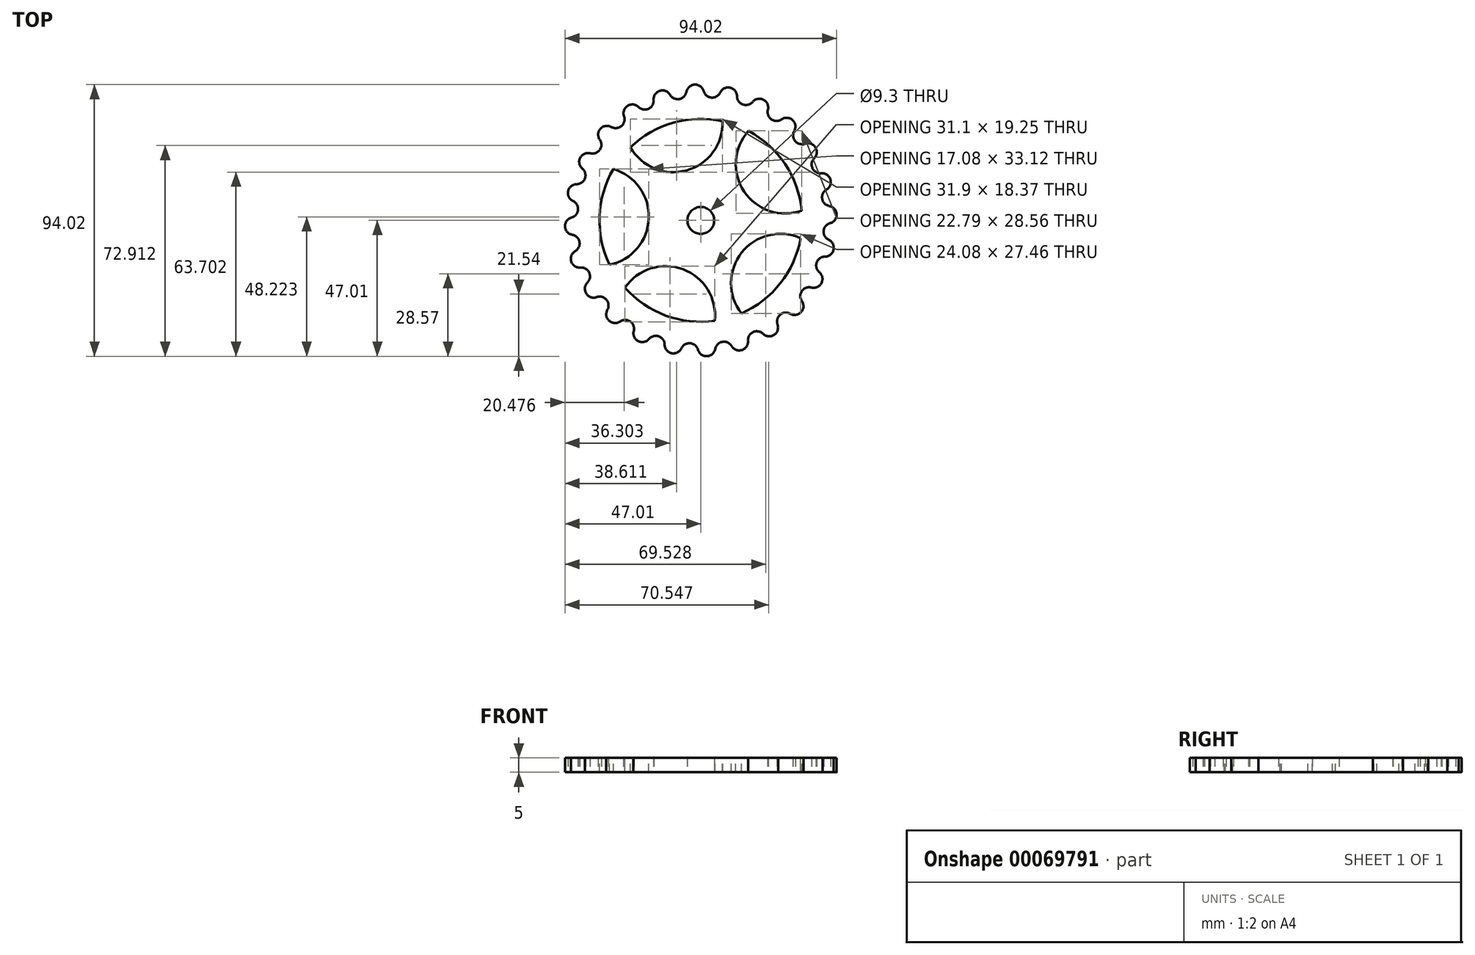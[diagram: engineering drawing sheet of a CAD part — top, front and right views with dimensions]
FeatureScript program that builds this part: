
annotation { "Feature Type Name" : "Feature", "Feature Type Description" : "" }
export const myFeature = defineFeature(function(context is Context, id is Id, definition is map)
    precondition{}
    {
        {
            var Q0;
            Q0=qCreatedBy(makeId("Top.planeOp"),FACE);
            var sketch = newSketch(context, id + "F0", { "sketchPlane" : qUnion([Q0])});
            skArc(sketch, "E0", {"start": v(0.98, 44.76) * mm, "mid": v(-0.17, 46.42) * mm, "end": v(-2.1, 47) * mm});
            skArc(sketch, "E1", {"start": v(0.98, 44.76) * mm, "mid": v(1.97, 43.21) * mm, "end": v(3.67, 42.51) * mm});
            skLineSegment(sketch, "E2", {"start": v(0, 0) * mm, "end": v(3.93, 45.56) * mm, "construction": true});
            skLineSegment(sketch, "E3", {"start": v(0, 0) * mm, "end": v(-1.97, 43.95) * mm, "construction": true});
            skLineSegment(sketch, "E4", {"start": v(-1.97, 43.95) * mm, "end": v(-2.18, 48.5) * mm, "construction": true});
            skArc(sketch, "E5.MirrorCS", {"start": v(6.7, 44.26) * mm, "mid": v(5.46, 42.91) * mm, "end": v(3.67, 42.51) * mm});
            skArc(sketch, "E6.MirrorCS", {"start": v(6.7, 44.26) * mm, "mid": v(8.12, 45.7) * mm, "end": v(10.13, 45.95) * mm});
            skArc(sketch, "E7.1.0", {"start": v(-10.64, 43.49) * mm, "mid": v(-12.18, 44.8) * mm, "end": v(-14.2, 44.86) * mm});
            skArc(sketch, "E7.1.1", {"start": v(-10.64, 43.49) * mm, "mid": v(-9.28, 42.25) * mm, "end": v(-7.46, 42.02) * mm});
            skArc(sketch, "E7.1.2", {"start": v(-4.98, 44.49) * mm, "mid": v(-5.83, 42.86) * mm, "end": v(-7.46, 42.02) * mm});
            skArc(sketch, "E7.1.3", {"start": v(-4.98, 44.49) * mm, "mid": v(-3.99, 46.25) * mm, "end": v(-2.1, 47) * mm});
            skArc(sketch, "E7.2.0", {"start": v(-21.53, 39.25) * mm, "mid": v(-23.36, 40.12) * mm, "end": v(-25.33, 39.66) * mm});
            skArc(sketch, "E7.2.1", {"start": v(-21.53, 39.25) * mm, "mid": v(-19.9, 38.4) * mm, "end": v(-18.08, 38.65) * mm});
            skArc(sketch, "E7.2.2", {"start": v(-16.33, 41.68) * mm, "mid": v(-16.73, 39.9) * mm, "end": v(-18.08, 38.65) * mm});
            skArc(sketch, "E7.2.3", {"start": v(-16.33, 41.68) * mm, "mid": v(-15.82, 43.65) * mm, "end": v(-14.2, 44.86) * mm});
            skArc(sketch, "E7.3.0", {"start": v(-30.96, 32.34) * mm, "mid": v(-32.95, 32.7) * mm, "end": v(-34.73, 31.75) * mm});
            skArc(sketch, "E7.3.1", {"start": v(-30.96, 32.34) * mm, "mid": v(-29.16, 31.95) * mm, "end": v(-27.47, 32.66) * mm});
            skArc(sketch, "E7.3.2", {"start": v(-26.56, 36.04) * mm, "mid": v(-26.48, 34.2) * mm, "end": v(-27.47, 32.66) * mm});
            skArc(sketch, "E7.3.3", {"start": v(-26.56, 36.04) * mm, "mid": v(-26.58, 38.06) * mm, "end": v(-25.33, 39.66) * mm});
            skArc(sketch, "E7.4.0", {"start": v(-38.27, 23.23) * mm, "mid": v(-40.29, 23.07) * mm, "end": v(-41.76, 21.68) * mm});
            skArc(sketch, "E7.4.1", {"start": v(-38.27, 23.23) * mm, "mid": v(-36.44, 23.31) * mm, "end": v(-34.98, 24.43) * mm});
            skArc(sketch, "E7.4.2", {"start": v(-34.98, 27.94) * mm, "mid": v(-34.43, 26.18) * mm, "end": v(-34.98, 24.43) * mm});
            skArc(sketch, "E7.4.3", {"start": v(-34.98, 27.94) * mm, "mid": v(-35.53, 29.89) * mm, "end": v(-34.73, 31.75) * mm});
            skArc(sketch, "E7.5.0", {"start": v(-42.98, 12.53) * mm, "mid": v(-44.89, 11.85) * mm, "end": v(-45.95, 10.13) * mm});
            skArc(sketch, "E7.5.1", {"start": v(-42.98, 12.53) * mm, "mid": v(-41.23, 13.09) * mm, "end": v(-40.12, 14.55) * mm});
            skArc(sketch, "E7.5.2", {"start": v(-41.02, 17.93) * mm, "mid": v(-40.04, 16.38) * mm, "end": v(-40.12, 14.55) * mm});
            skArc(sketch, "E7.5.3", {"start": v(-41.02, 17.93) * mm, "mid": v(-42.05, 19.67) * mm, "end": v(-41.76, 21.68) * mm});
            skArc(sketch, "E7.6.0", {"start": v(-44.76, 0.98) * mm, "mid": v(-46.42, -0.17) * mm, "end": v(-47, -2.1) * mm});
            skArc(sketch, "E7.6.1", {"start": v(-44.76, 0.98) * mm, "mid": v(-43.21, 1.97) * mm, "end": v(-42.51, 3.67) * mm});
            skArc(sketch, "E7.6.2", {"start": v(-44.26, 6.7) * mm, "mid": v(-42.91, 5.46) * mm, "end": v(-42.51, 3.67) * mm});
            skArc(sketch, "E7.6.3", {"start": v(-44.26, 6.7) * mm, "mid": v(-45.7, 8.12) * mm, "end": v(-45.95, 10.13) * mm});
            skArc(sketch, "E7.7.0", {"start": v(-43.49, -10.64) * mm, "mid": v(-44.8, -12.18) * mm, "end": v(-44.86, -14.2) * mm});
            skArc(sketch, "E7.7.1", {"start": v(-43.49, -10.64) * mm, "mid": v(-42.25, -9.28) * mm, "end": v(-42.02, -7.46) * mm});
            skArc(sketch, "E7.7.2", {"start": v(-44.49, -4.98) * mm, "mid": v(-42.86, -5.83) * mm, "end": v(-42.02, -7.46) * mm});
            skArc(sketch, "E7.7.3", {"start": v(-44.49, -4.98) * mm, "mid": v(-46.25, -3.99) * mm, "end": v(-47, -2.1) * mm});
            skArc(sketch, "E7.8.0", {"start": v(-39.25, -21.53) * mm, "mid": v(-40.12, -23.36) * mm, "end": v(-39.66, -25.33) * mm});
            skArc(sketch, "E7.8.1", {"start": v(-39.25, -21.53) * mm, "mid": v(-38.4, -19.9) * mm, "end": v(-38.65, -18.08) * mm});
            skArc(sketch, "E7.8.2", {"start": v(-41.68, -16.33) * mm, "mid": v(-39.9, -16.73) * mm, "end": v(-38.65, -18.08) * mm});
            skArc(sketch, "E7.8.3", {"start": v(-41.68, -16.33) * mm, "mid": v(-43.65, -15.82) * mm, "end": v(-44.86, -14.2) * mm});
            skArc(sketch, "E7.9.0", {"start": v(-32.34, -30.96) * mm, "mid": v(-32.7, -32.95) * mm, "end": v(-31.75, -34.73) * mm});
            skArc(sketch, "E7.9.1", {"start": v(-32.34, -30.96) * mm, "mid": v(-31.95, -29.16) * mm, "end": v(-32.66, -27.47) * mm});
            skArc(sketch, "E7.9.2", {"start": v(-36.04, -26.56) * mm, "mid": v(-34.2, -26.48) * mm, "end": v(-32.66, -27.47) * mm});
            skArc(sketch, "E7.9.3", {"start": v(-36.04, -26.56) * mm, "mid": v(-38.06, -26.58) * mm, "end": v(-39.66, -25.33) * mm});
            skArc(sketch, "E7.10.0", {"start": v(-23.23, -38.27) * mm, "mid": v(-23.07, -40.29) * mm, "end": v(-21.68, -41.76) * mm});
            skArc(sketch, "E7.10.1", {"start": v(-23.23, -38.27) * mm, "mid": v(-23.31, -36.44) * mm, "end": v(-24.43, -34.98) * mm});
            skArc(sketch, "E7.10.2", {"start": v(-27.94, -34.98) * mm, "mid": v(-26.18, -34.43) * mm, "end": v(-24.43, -34.98) * mm});
            skArc(sketch, "E7.10.3", {"start": v(-27.94, -34.98) * mm, "mid": v(-29.89, -35.53) * mm, "end": v(-31.75, -34.73) * mm});
            skArc(sketch, "E7.11.0", {"start": v(-12.53, -42.98) * mm, "mid": v(-11.85, -44.89) * mm, "end": v(-10.13, -45.95) * mm});
            skArc(sketch, "E7.11.1", {"start": v(-12.53, -42.98) * mm, "mid": v(-13.09, -41.23) * mm, "end": v(-14.55, -40.12) * mm});
            skArc(sketch, "E7.11.2", {"start": v(-17.93, -41.02) * mm, "mid": v(-16.38, -40.04) * mm, "end": v(-14.55, -40.12) * mm});
            skArc(sketch, "E7.11.3", {"start": v(-17.93, -41.02) * mm, "mid": v(-19.67, -42.05) * mm, "end": v(-21.68, -41.76) * mm});
            skArc(sketch, "E7.12.0", {"start": v(-0.98, -44.76) * mm, "mid": v(0.17, -46.42) * mm, "end": v(2.1, -47) * mm});
            skArc(sketch, "E7.12.1", {"start": v(-0.98, -44.76) * mm, "mid": v(-1.97, -43.21) * mm, "end": v(-3.67, -42.51) * mm});
            skArc(sketch, "E7.12.2", {"start": v(-6.7, -44.26) * mm, "mid": v(-5.46, -42.91) * mm, "end": v(-3.67, -42.51) * mm});
            skArc(sketch, "E7.12.3", {"start": v(-6.7, -44.26) * mm, "mid": v(-8.12, -45.7) * mm, "end": v(-10.13, -45.95) * mm});
            skArc(sketch, "E7.13.0", {"start": v(10.64, -43.49) * mm, "mid": v(12.18, -44.8) * mm, "end": v(14.2, -44.86) * mm});
            skArc(sketch, "E7.13.1", {"start": v(10.64, -43.49) * mm, "mid": v(9.28, -42.25) * mm, "end": v(7.46, -42.02) * mm});
            skArc(sketch, "E7.13.2", {"start": v(4.98, -44.49) * mm, "mid": v(5.83, -42.86) * mm, "end": v(7.46, -42.02) * mm});
            skArc(sketch, "E7.13.3", {"start": v(4.98, -44.49) * mm, "mid": v(3.99, -46.25) * mm, "end": v(2.1, -47) * mm});
            skArc(sketch, "E7.14.0", {"start": v(21.53, -39.25) * mm, "mid": v(23.36, -40.12) * mm, "end": v(25.33, -39.66) * mm});
            skArc(sketch, "E7.14.1", {"start": v(21.53, -39.25) * mm, "mid": v(19.9, -38.4) * mm, "end": v(18.08, -38.65) * mm});
            skArc(sketch, "E7.14.2", {"start": v(16.33, -41.68) * mm, "mid": v(16.73, -39.9) * mm, "end": v(18.08, -38.65) * mm});
            skArc(sketch, "E7.14.3", {"start": v(16.33, -41.68) * mm, "mid": v(15.82, -43.65) * mm, "end": v(14.2, -44.86) * mm});
            skArc(sketch, "E7.15.0", {"start": v(30.96, -32.34) * mm, "mid": v(32.95, -32.7) * mm, "end": v(34.73, -31.75) * mm});
            skArc(sketch, "E7.15.1", {"start": v(30.96, -32.34) * mm, "mid": v(29.16, -31.95) * mm, "end": v(27.47, -32.66) * mm});
            skArc(sketch, "E7.15.2", {"start": v(26.56, -36.04) * mm, "mid": v(26.48, -34.2) * mm, "end": v(27.47, -32.66) * mm});
            skArc(sketch, "E7.15.3", {"start": v(26.56, -36.04) * mm, "mid": v(26.58, -38.06) * mm, "end": v(25.33, -39.66) * mm});
            skArc(sketch, "E7.16.0", {"start": v(38.27, -23.23) * mm, "mid": v(40.29, -23.07) * mm, "end": v(41.76, -21.68) * mm});
            skArc(sketch, "E7.16.1", {"start": v(38.27, -23.23) * mm, "mid": v(36.44, -23.31) * mm, "end": v(34.98, -24.43) * mm});
            skArc(sketch, "E7.16.2", {"start": v(34.98, -27.94) * mm, "mid": v(34.43, -26.18) * mm, "end": v(34.98, -24.43) * mm});
            skArc(sketch, "E7.16.3", {"start": v(34.98, -27.94) * mm, "mid": v(35.53, -29.89) * mm, "end": v(34.73, -31.75) * mm});
            skArc(sketch, "E7.17.0", {"start": v(42.98, -12.53) * mm, "mid": v(44.89, -11.85) * mm, "end": v(45.95, -10.13) * mm});
            skArc(sketch, "E7.17.1", {"start": v(42.98, -12.53) * mm, "mid": v(41.23, -13.09) * mm, "end": v(40.12, -14.55) * mm});
            skArc(sketch, "E7.17.2", {"start": v(41.02, -17.93) * mm, "mid": v(40.04, -16.38) * mm, "end": v(40.12, -14.55) * mm});
            skArc(sketch, "E7.17.3", {"start": v(41.02, -17.93) * mm, "mid": v(42.05, -19.67) * mm, "end": v(41.76, -21.68) * mm});
            skArc(sketch, "E7.18.0", {"start": v(44.76, -0.98) * mm, "mid": v(46.42, 0.17) * mm, "end": v(47, 2.1) * mm});
            skArc(sketch, "E7.18.1", {"start": v(44.76, -0.98) * mm, "mid": v(43.21, -1.97) * mm, "end": v(42.51, -3.67) * mm});
            skArc(sketch, "E7.18.2", {"start": v(44.26, -6.7) * mm, "mid": v(42.91, -5.46) * mm, "end": v(42.51, -3.67) * mm});
            skArc(sketch, "E7.18.3", {"start": v(44.26, -6.7) * mm, "mid": v(45.7, -8.12) * mm, "end": v(45.95, -10.13) * mm});
            skArc(sketch, "E7.19.0", {"start": v(43.49, 10.64) * mm, "mid": v(44.8, 12.18) * mm, "end": v(44.86, 14.2) * mm});
            skArc(sketch, "E7.19.1", {"start": v(43.49, 10.64) * mm, "mid": v(42.25, 9.28) * mm, "end": v(42.02, 7.46) * mm});
            skArc(sketch, "E7.19.2", {"start": v(44.49, 4.98) * mm, "mid": v(42.86, 5.83) * mm, "end": v(42.02, 7.46) * mm});
            skArc(sketch, "E7.19.3", {"start": v(44.49, 4.98) * mm, "mid": v(46.25, 3.99) * mm, "end": v(47, 2.1) * mm});
            skArc(sketch, "E7.20.0", {"start": v(39.25, 21.53) * mm, "mid": v(40.12, 23.36) * mm, "end": v(39.66, 25.33) * mm});
            skArc(sketch, "E7.20.1", {"start": v(39.25, 21.53) * mm, "mid": v(38.4, 19.9) * mm, "end": v(38.65, 18.08) * mm});
            skArc(sketch, "E7.20.2", {"start": v(41.68, 16.33) * mm, "mid": v(39.9, 16.73) * mm, "end": v(38.65, 18.08) * mm});
            skArc(sketch, "E7.20.3", {"start": v(41.68, 16.33) * mm, "mid": v(43.65, 15.82) * mm, "end": v(44.86, 14.2) * mm});
            skArc(sketch, "E7.21.0", {"start": v(32.34, 30.96) * mm, "mid": v(32.7, 32.95) * mm, "end": v(31.75, 34.73) * mm});
            skArc(sketch, "E7.21.1", {"start": v(32.34, 30.96) * mm, "mid": v(31.95, 29.16) * mm, "end": v(32.66, 27.47) * mm});
            skArc(sketch, "E7.21.2", {"start": v(36.04, 26.56) * mm, "mid": v(34.2, 26.48) * mm, "end": v(32.66, 27.47) * mm});
            skArc(sketch, "E7.21.3", {"start": v(36.04, 26.56) * mm, "mid": v(38.06, 26.58) * mm, "end": v(39.66, 25.33) * mm});
            skArc(sketch, "E7.22.0", {"start": v(23.23, 38.27) * mm, "mid": v(23.07, 40.29) * mm, "end": v(21.68, 41.76) * mm});
            skArc(sketch, "E7.22.1", {"start": v(23.23, 38.27) * mm, "mid": v(23.31, 36.44) * mm, "end": v(24.43, 34.98) * mm});
            skArc(sketch, "E7.22.2", {"start": v(27.94, 34.98) * mm, "mid": v(26.18, 34.43) * mm, "end": v(24.43, 34.98) * mm});
            skArc(sketch, "E7.22.3", {"start": v(27.94, 34.98) * mm, "mid": v(29.89, 35.53) * mm, "end": v(31.75, 34.73) * mm});
            skArc(sketch, "E7.23.0", {"start": v(12.53, 42.98) * mm, "mid": v(11.85, 44.89) * mm, "end": v(10.13, 45.95) * mm});
            skArc(sketch, "E7.23.1", {"start": v(12.53, 42.98) * mm, "mid": v(13.09, 41.23) * mm, "end": v(14.55, 40.12) * mm});
            skArc(sketch, "E7.23.2", {"start": v(17.93, 41.02) * mm, "mid": v(16.38, 40.04) * mm, "end": v(14.55, 40.12) * mm});
            skArc(sketch, "E7.23.3", {"start": v(17.93, 41.02) * mm, "mid": v(19.67, 42.05) * mm, "end": v(21.68, 41.76) * mm});
            skPoint(sketch, "E7.center", {"position": v(0, 0) * mm});
            skSolve(sketch);
        }
        {
            var Q0;
            Q0=makeQuery(id+"F0.imprint","IMPRINT",FACE,{"disambiguationData":[TD([[makeQuery(id+"F0.imprint","IMPRINT",EDGE,{"derivedFrom":sQuery(id+"F0.wireOp",EDGE,"E0")}),1.0]])]});
            extrude(context, id + "F1", {"entities" : qUnion([Q0]), "depth" : 5 * mm});
        }
        {
            var Q0;
            Q0=qCreatedBy(makeId("Top.planeOp"),FACE);
            var sketch = newSketch(context, id + "F2", { "sketchPlane" : qUnion([Q0])});
            skCircle(sketch, "E8", {"center": v(0, 0) * mm, "radius": 4.65 * mm});
            skSolve(sketch);
        }
        {
            var Q0;
            Q0 = qSketchRegion(id + "F2", true);
            extrude(context, id + "F3", {"entities" : qUnion([Q0]), "operationType" : NewBodyOperationType.REMOVE, "depth" : 25 * mm});
        }
        {
            var Q0;
            Q0=makeQuery(id+"F1.opExtrude","CAP_FACE",FACE,{"disambiguationData":[OSD([sQuery(id+"F0.wireOp",EDGE,"E0"),sQuery(id+"F0.wireOp",EDGE,"E1"),sQuery(id+"F0.wireOp",EDGE,"E5.MirrorCS"),sQuery(id+"F0.wireOp",EDGE,"E6.MirrorCS"),sQuery(id+"F0.wireOp",EDGE,"E7.1.0"),sQuery(id+"F0.wireOp",EDGE,"E7.1.1"),sQuery(id+"F0.wireOp",EDGE,"E7.1.2"),sQuery(id+"F0.wireOp",EDGE,"E7.1.3"),sQuery(id+"F0.wireOp",EDGE,"E7.2.0"),sQuery(id+"F0.wireOp",EDGE,"E7.2.1"),sQuery(id+"F0.wireOp",EDGE,"E7.2.2"),sQuery(id+"F0.wireOp",EDGE,"E7.2.3"),sQuery(id+"F0.wireOp",EDGE,"E7.3.0"),sQuery(id+"F0.wireOp",EDGE,"E7.3.1"),sQuery(id+"F0.wireOp",EDGE,"E7.3.2"),sQuery(id+"F0.wireOp",EDGE,"E7.3.3"),sQuery(id+"F0.wireOp",EDGE,"E7.4.0"),sQuery(id+"F0.wireOp",EDGE,"E7.4.1"),sQuery(id+"F0.wireOp",EDGE,"E7.4.2"),sQuery(id+"F0.wireOp",EDGE,"E7.4.3"),sQuery(id+"F0.wireOp",EDGE,"E7.5.0"),sQuery(id+"F0.wireOp",EDGE,"E7.5.1"),sQuery(id+"F0.wireOp",EDGE,"E7.5.2"),sQuery(id+"F0.wireOp",EDGE,"E7.5.3"),sQuery(id+"F0.wireOp",EDGE,"E7.6.0"),sQuery(id+"F0.wireOp",EDGE,"E7.6.1"),sQuery(id+"F0.wireOp",EDGE,"E7.6.2"),sQuery(id+"F0.wireOp",EDGE,"E7.6.3"),sQuery(id+"F0.wireOp",EDGE,"E7.7.0"),sQuery(id+"F0.wireOp",EDGE,"E7.7.1"),sQuery(id+"F0.wireOp",EDGE,"E7.7.2"),sQuery(id+"F0.wireOp",EDGE,"E7.7.3"),sQuery(id+"F0.wireOp",EDGE,"E7.8.0"),sQuery(id+"F0.wireOp",EDGE,"E7.8.1"),sQuery(id+"F0.wireOp",EDGE,"E7.8.2"),sQuery(id+"F0.wireOp",EDGE,"E7.8.3"),sQuery(id+"F0.wireOp",EDGE,"E7.9.0"),sQuery(id+"F0.wireOp",EDGE,"E7.9.1"),sQuery(id+"F0.wireOp",EDGE,"E7.9.2"),sQuery(id+"F0.wireOp",EDGE,"E7.9.3"),sQuery(id+"F0.wireOp",EDGE,"E7.10.0"),sQuery(id+"F0.wireOp",EDGE,"E7.10.1"),sQuery(id+"F0.wireOp",EDGE,"E7.10.2"),sQuery(id+"F0.wireOp",EDGE,"E7.10.3"),sQuery(id+"F0.wireOp",EDGE,"E7.11.0"),sQuery(id+"F0.wireOp",EDGE,"E7.11.1"),sQuery(id+"F0.wireOp",EDGE,"E7.11.2"),sQuery(id+"F0.wireOp",EDGE,"E7.11.3"),sQuery(id+"F0.wireOp",EDGE,"E7.12.0"),sQuery(id+"F0.wireOp",EDGE,"E7.12.1"),sQuery(id+"F0.wireOp",EDGE,"E7.12.2"),sQuery(id+"F0.wireOp",EDGE,"E7.12.3"),sQuery(id+"F0.wireOp",EDGE,"E7.13.0"),sQuery(id+"F0.wireOp",EDGE,"E7.13.1"),sQuery(id+"F0.wireOp",EDGE,"E7.13.2"),sQuery(id+"F0.wireOp",EDGE,"E7.13.3"),sQuery(id+"F0.wireOp",EDGE,"E7.14.0"),sQuery(id+"F0.wireOp",EDGE,"E7.14.1"),sQuery(id+"F0.wireOp",EDGE,"E7.14.2"),sQuery(id+"F0.wireOp",EDGE,"E7.14.3"),sQuery(id+"F0.wireOp",EDGE,"E7.15.0"),sQuery(id+"F0.wireOp",EDGE,"E7.15.1"),sQuery(id+"F0.wireOp",EDGE,"E7.15.2"),sQuery(id+"F0.wireOp",EDGE,"E7.15.3"),sQuery(id+"F0.wireOp",EDGE,"E7.16.0"),sQuery(id+"F0.wireOp",EDGE,"E7.16.1"),sQuery(id+"F0.wireOp",EDGE,"E7.16.2"),sQuery(id+"F0.wireOp",EDGE,"E7.16.3"),sQuery(id+"F0.wireOp",EDGE,"E7.17.0"),sQuery(id+"F0.wireOp",EDGE,"E7.17.1"),sQuery(id+"F0.wireOp",EDGE,"E7.17.2"),sQuery(id+"F0.wireOp",EDGE,"E7.17.3"),sQuery(id+"F0.wireOp",EDGE,"E7.18.0"),sQuery(id+"F0.wireOp",EDGE,"E7.18.1"),sQuery(id+"F0.wireOp",EDGE,"E7.18.2"),sQuery(id+"F0.wireOp",EDGE,"E7.18.3"),sQuery(id+"F0.wireOp",EDGE,"E7.19.0"),sQuery(id+"F0.wireOp",EDGE,"E7.19.1"),sQuery(id+"F0.wireOp",EDGE,"E7.19.2"),sQuery(id+"F0.wireOp",EDGE,"E7.19.3"),sQuery(id+"F0.wireOp",EDGE,"E7.20.0"),sQuery(id+"F0.wireOp",EDGE,"E7.20.1"),sQuery(id+"F0.wireOp",EDGE,"E7.20.2"),sQuery(id+"F0.wireOp",EDGE,"E7.20.3"),sQuery(id+"F0.wireOp",EDGE,"E7.21.0"),sQuery(id+"F0.wireOp",EDGE,"E7.21.1"),sQuery(id+"F0.wireOp",EDGE,"E7.21.2"),sQuery(id+"F0.wireOp",EDGE,"E7.21.3"),sQuery(id+"F0.wireOp",EDGE,"E7.22.0"),sQuery(id+"F0.wireOp",EDGE,"E7.22.1"),sQuery(id+"F0.wireOp",EDGE,"E7.22.2"),sQuery(id+"F0.wireOp",EDGE,"E7.22.3"),sQuery(id+"F0.wireOp",EDGE,"E7.23.0"),sQuery(id+"F0.wireOp",EDGE,"E7.23.1"),sQuery(id+"F0.wireOp",EDGE,"E7.23.2"),sQuery(id+"F0.wireOp",EDGE,"E7.23.3")])],"isStart":false});
            var sketch = newSketch(context, id + "F4", { "sketchPlane" : qUnion([Q0])});
            skArc(sketch, "E9", {"start": v(14.04, -32.17) * mm, "mid": v(27.57, -21.73) * mm, "end": v(34.56, -6.14) * mm});
            skArc(sketch, "E10", {"start": v(34.56, -6.14) * mm, "mid": v(14.14, -11.15) * mm, "end": v(14.04, -32.17) * mm});
            skArc(sketch, "E11.1.0", {"start": v(16.52, 30.97) * mm, "mid": v(14.97, 10) * mm, "end": v(34.93, 3.4) * mm});
            skArc(sketch, "E11.2.0", {"start": v(-24.35, 25.28) * mm, "mid": v(-4.89, 17.33) * mm, "end": v(7.55, 34.28) * mm});
            skArc(sketch, "E11.3.0", {"start": v(-31.57, -15.35) * mm, "mid": v(-18, 0.7) * mm, "end": v(-30.27, 17.78) * mm});
            skArc(sketch, "E11.4.0", {"start": v(4.84, -34.76) * mm, "mid": v(-6.23, -16.9) * mm, "end": v(-26.26, -23.3) * mm});
            skArc(sketch, "E12.trimOffspring", {"start": v(-26.26, -23.3) * mm, "mid": v(-12.15, -32.93) * mm, "end": v(4.84, -34.76) * mm});
            skArc(sketch, "E13.trimOffspring", {"start": v(-30.27, 17.78) * mm, "mid": v(-35.07, 1.38) * mm, "end": v(-31.57, -15.35) * mm});
            skArc(sketch, "E14.trimOffspring", {"start": v(7.55, 34.28) * mm, "mid": v(-9.53, 33.78) * mm, "end": v(-24.35, 25.28) * mm});
            skArc(sketch, "E15.trimOffspring", {"start": v(34.93, 3.4) * mm, "mid": v(29.18, 19.5) * mm, "end": v(16.52, 30.97) * mm});
            skSolve(sketch);
        }
        {
            var Q0;
            Q0=makeQuery(id+"F4.imprint","IMPRINT",FACE,{"disambiguationData":[TD([[makeQuery(id+"F4.imprint","IMPRINT",EDGE,{"derivedFrom":sQuery(id+"F4.wireOp",EDGE,"E9")}),1.0]])]});
            var Q1;
            Q1=makeQuery(id+"F4.imprint","IMPRINT",FACE,{"disambiguationData":[TD([[makeQuery(id+"F4.imprint","IMPRINT",EDGE,{"derivedFrom":sQuery(id+"F4.wireOp",EDGE,"E11.4.0")}),1.0]])]});
            var Q2;
            Q2=makeQuery(id+"F4.imprint","IMPRINT",FACE,{"disambiguationData":[TD([[makeQuery(id+"F4.imprint","IMPRINT",EDGE,{"derivedFrom":sQuery(id+"F4.wireOp",EDGE,"E11.3.0")}),1.0]])]});
            var Q3;
            Q3=makeQuery(id+"F4.imprint","IMPRINT",FACE,{"disambiguationData":[TD([[makeQuery(id+"F4.imprint","IMPRINT",EDGE,{"derivedFrom":sQuery(id+"F4.wireOp",EDGE,"E11.2.0")}),1.0]])]});
            var Q4;
            Q4=makeQuery(id+"F4.imprint","IMPRINT",FACE,{"disambiguationData":[TD([[makeQuery(id+"F4.imprint","IMPRINT",EDGE,{"derivedFrom":sQuery(id+"F4.wireOp",EDGE,"E11.1.0")}),1.0]])]});
            extrude(context, id + "F5", {"entities" : qUnion([Q0, Q1, Q2, Q3, Q4]), "operationType" : NewBodyOperationType.REMOVE, "oppositeDirection" : true, "depth" : 25 * mm});
        }
    });
